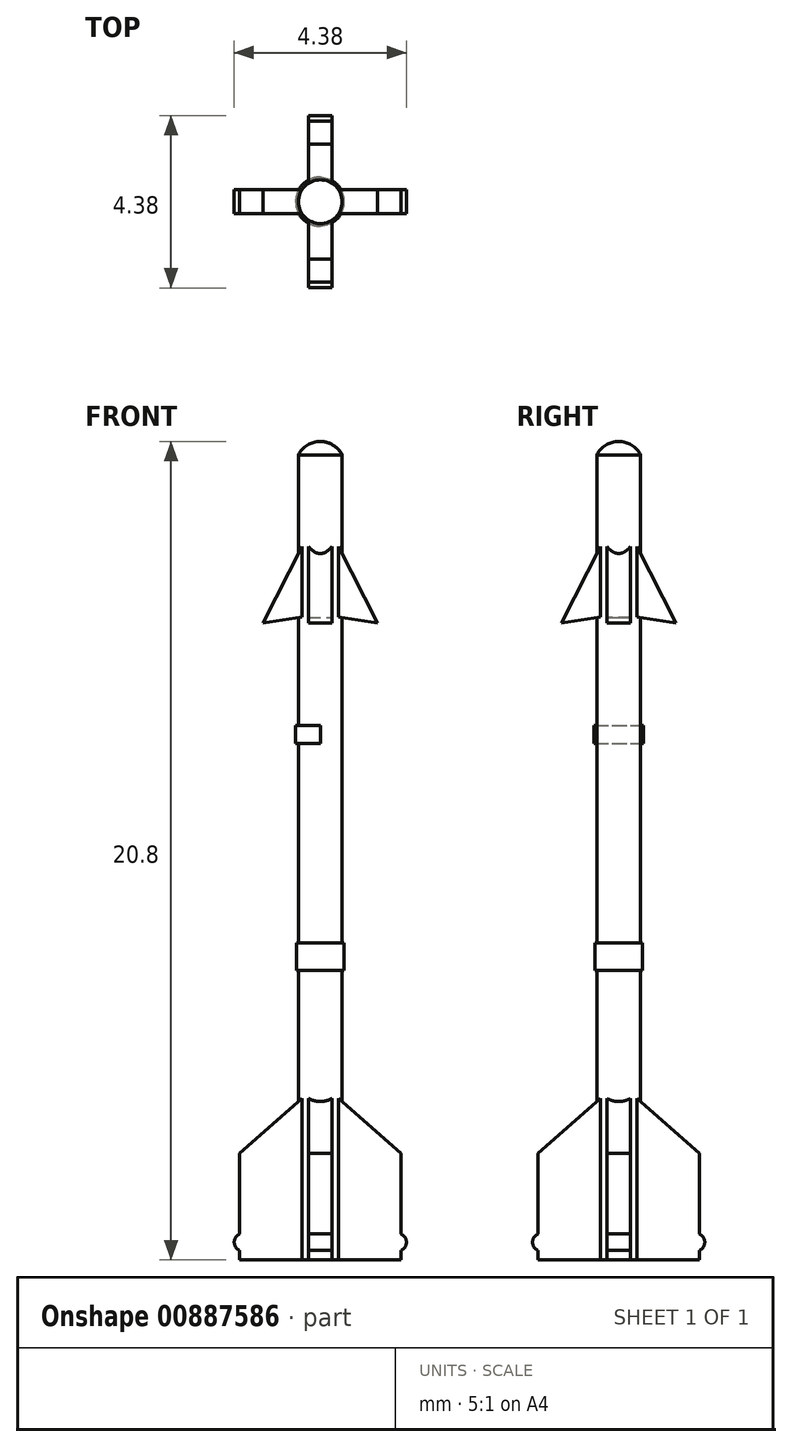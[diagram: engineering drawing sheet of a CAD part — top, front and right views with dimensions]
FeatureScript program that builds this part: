
annotation { "Feature Type Name" : "Feature", "Feature Type Description" : "" }
export const myFeature = defineFeature(function(context is Context, id is Id, definition is map)
    precondition{}
    {
        {
            var Q0;
            Q0=qCreatedBy(makeId("Front.planeOp"),FACE);
            var sketch = newSketch(context, id + "F0", { "sketchPlane" : qUnion([Q0])});
            skLineSegment(sketch, "E0", {"start": v(0, 0) * mm, "end": v(0.56, 0) * mm});
            skLineSegment(sketch, "E1", {"start": v(0.56, 0) * mm, "end": v(0.56, 7.36) * mm});
            skLineSegment(sketch, "E2", {"start": v(0.56, 7.36) * mm, "end": v(0.6, 7.36) * mm});
            skLineSegment(sketch, "E3", {"start": v(0.6, 7.36) * mm, "end": v(0.6, 8.06) * mm});
            skLineSegment(sketch, "E4", {"start": v(0.6, 8.06) * mm, "end": v(0.56, 8.06) * mm});
            skLineSegment(sketch, "E5", {"start": v(0.56, 8.06) * mm, "end": v(0.56, 20.45) * mm});
            skLineSegment(sketch, "E6", {"start": v(0, 20.8) * mm, "end": v(0, 0) * mm});
            skLineSegment(sketch, "E7", {"start": v(0, 20.8) * mm, "end": v(1.97, 20.8) * mm, "construction": true});
            skArc(sketch, "E8", {"start": v(0.56, 20.45) * mm, "mid": v(0.33, 20.7) * mm, "end": v(0, 20.8) * mm});
            skSolve(sketch);
        }
        {
            var Q0;
            Q0 = qSketchRegion(id + "F0", true);
            var Q1;
            Q1=sQuery(id+"F0.wireOp",EDGE,"E6");
            revolve(context, id + "F1", {"surfaceOperationType" : NewSurfaceOperationType.NEW, "entities" : qUnion([Q0]), "axis" : qUnion([Q1]), "revolveType" : RevolveType.FULL});
        }
        {
            var Q0;
            Q0=qCreatedBy(makeId("Front.planeOp"),FACE);
            var sketch = newSketch(context, id + "F2", { "sketchPlane" : qUnion([Q0])});
            skLineSegment(sketch, "E9", {"start": v(2.05, 0) * mm, "end": v(0, 0) * mm});
            skLineSegment(sketch, "E10", {"start": v(2.05, 0) * mm, "end": v(2.05, 0.24) * mm});
            skLineSegment(sketch, "E11", {"start": v(2.05, 2.7) * mm, "end": v(0.4, 4.17) * mm});
            skLineSegment(sketch, "E12", {"start": v(0.4, 4.17) * mm, "end": v(0.4, 16.34) * mm});
            skLineSegment(sketch, "E13", {"start": v(0.4, 16.34) * mm, "end": v(1.46, 16.18) * mm});
            skLineSegment(sketch, "E14", {"start": v(1.46, 16.18) * mm, "end": v(0, 19.04) * mm});
            skLineSegment(sketch, "E15", {"start": v(0, 19.04) * mm, "end": v(0, 0) * mm});
            skLineSegment(sketch, "E16.0", {"start": v(-0.56, 20.45) * mm, "end": v(0.56, 20.45) * mm});
            skLineSegment(sketch, "E17", {"start": v(0.56, 20.45) * mm, "end": v(0.56, -2.61) * mm, "construction": true});
            skPoint(sketch, "E18", {"position": v(0.56, 4.03) * mm});
            skPoint(sketch, "E19", {"position": v(0.56, 16.32) * mm});
            skPoint(sketch, "E20", {"position": v(0.56, 17.95) * mm});
            skArc(sketch, "E21", {"start": v(2.05, 0.24) * mm, "mid": v(2.19, 0.45) * mm, "end": v(2.05, 0.66) * mm});
            skLineSegment(sketch, "E22.trimOffspring", {"start": v(2.05, 0.66) * mm, "end": v(2.05, 2.7) * mm});
            skSolve(sketch);
        }
        {
            var Q0;
            Q0 = qSketchRegion(id + "F2", true);
            extrude(context, id + "F3", {"entities" : qUnion([Q0]), "operationType" : NewBodyOperationType.ADD, "depth" : .6 * mm, "offsetDistance" : 25 * mm, "symmetric" : true});
        }
        {
            var Q0;
            Q0=makeQuery(id+"F1.opRevolve","SWEPT_BODY",BODY,{"disambiguationData":[OSD([sQuery(id+"F0.wireOp",EDGE,"E0"),sQuery(id+"F0.wireOp",EDGE,"E1"),sQuery(id+"F0.wireOp",EDGE,"E2"),sQuery(id+"F0.wireOp",EDGE,"E3"),sQuery(id+"F0.wireOp",EDGE,"E4"),sQuery(id+"F0.wireOp",EDGE,"E5"),sQuery(id+"F0.wireOp",EDGE,"E6"),sQuery(id+"F0.wireOp",EDGE,"E8")])]});
            var Q1;
            Q1=makeQuery(id+"F1.opRevolve","SWEPT_FACE",FACE,{"disambiguationData":[OSD([sQuery(id+"F0.wireOp",EDGE,"E5")])]});
            circularPattern(context, id + "F4", {"operationType" : NewBodyOperationType.ADD, "entities" : qUnion([Q0]), "axis" : qUnion([Q1]), "angle" : 360 * degree, "instanceCount" : 4, "equalSpace" : true, "computeTransformsWithoutBuiltin" : true});
        }
        {
            var Q0;
            Q0=qCreatedBy(makeId("Front.planeOp"),FACE);
            var sketch = newSketch(context, id + "F5", { "sketchPlane" : qUnion([Q0])});
            skLineSegment(sketch, "E23.bottom", {"start": v(0, 13.12) * mm, "end": v(-0.63, 13.12) * mm});
            skLineSegment(sketch, "E23.top", {"start": v(0, 13.58) * mm, "end": v(-0.63, 13.58) * mm});
            skLineSegment(sketch, "E23.left", {"start": v(0, 13.12) * mm, "end": v(0, 13.58) * mm});
            skLineSegment(sketch, "E23.right", {"start": v(-0.63, 13.12) * mm, "end": v(-0.63, 13.58) * mm});
            skSolve(sketch);
        }
        {
            var Q0;
            Q0 = qSketchRegion(id + "F5", true);
            var Q1;
            Q1=makeQuery(id+"F1.opRevolve","SWEPT_FACE",FACE,{"disambiguationData":[OSD([sQuery(id+"F0.wireOp",EDGE,"E5")])]});
            revolve(context, id + "F6", {"operationType" : NewBodyOperationType.ADD, "surfaceOperationType" : NewSurfaceOperationType.NEW, "entities" : qUnion([Q0]), "axis" : qUnion([Q1]), "revolveType" : RevolveType.SYMMETRIC, "angle" : 180 * degree});
        }
    });
